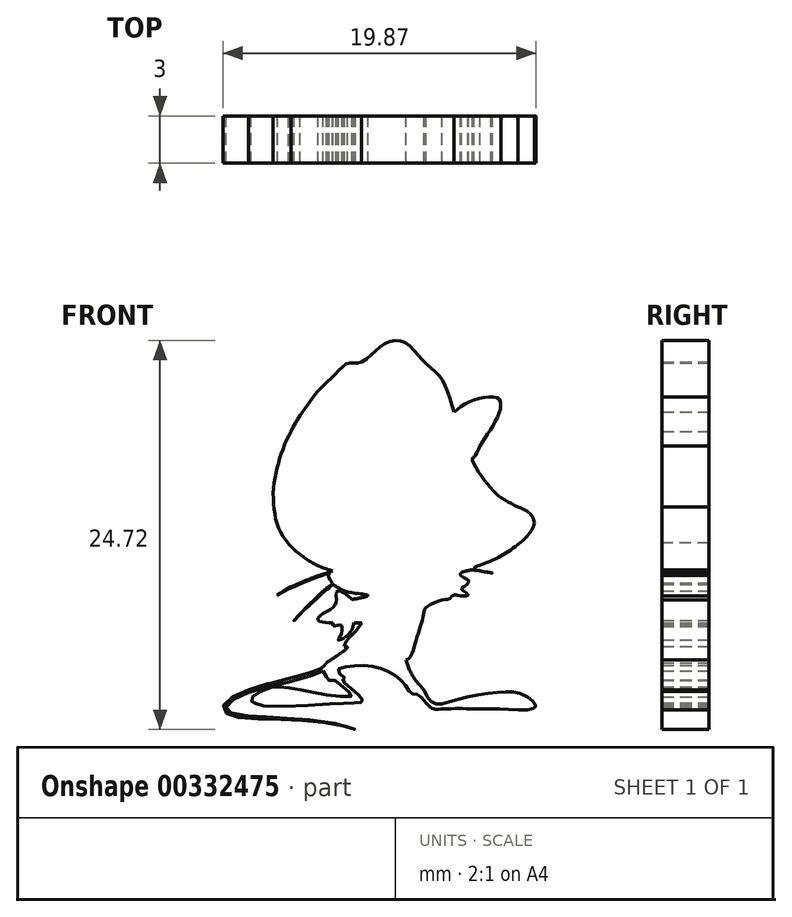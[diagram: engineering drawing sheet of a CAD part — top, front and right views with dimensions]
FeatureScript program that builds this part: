
annotation { "Feature Type Name" : "Feature", "Feature Type Description" : "" }
export const myFeature = defineFeature(function(context is Context, id is Id, definition is map)
    precondition{}
    {
        {
            var Q0;
            Q0=qCreatedBy(makeId("Front.planeOp"),FACE);
            var sketch = newSketch(context, id + "F0", { "sketchPlane" : qUnion([Q0])});
            skLineSegment(sketch, "E0", {"start": v(0, -15.9) * mm, "end": v(0, -15.3) * mm});
            skLineSegment(sketch, "E1", {"start": v(0, -15.3) * mm, "end": v(10.5, -15.15) * mm});
            skLineSegment(sketch, "E2", {"start": v(-10.5, 9.26) * mm, "end": v(-10.5, 18.4) * mm});
            skLineSegment(sketch, "E3", {"start": v(-10.5, 18.4) * mm, "end": v(0, 18.4) * mm});
            skLineSegment(sketch, "E4", {"start": v(0, 18.4) * mm, "end": v(0, 15.3) * mm});
            skLineSegment(sketch, "E5", {"start": v(0, 15.3) * mm, "end": v(10.5, 15.3) * mm});
            skLineSegment(sketch, "E6", {"start": v(10.5, 15.3) * mm, "end": v(10.5, 9.26) * mm});
            skLineSegment(sketch, "E7", {"start": v(-33.45, 0) * mm, "end": v(30.2, 0) * mm});
            skLineSegment(sketch, "E8", {"start": v(0, -15.3) * mm, "end": v(0, -18.4) * mm});
            skLineSegment(sketch, "E9", {"start": v(0, -18.4) * mm, "end": v(-10.5, -18.4) * mm});
            skLineSegment(sketch, "E10", {"start": v(-10.5, -18.4) * mm, "end": v(-10.63, -9.1) * mm});
            skArc(sketch, "E11", {"start": v(-10.5, 9.26) * mm, "mid": v(-14, 0.1) * mm, "end": v(-10.63, -9.1) * mm});
            skLineSegment(sketch, "E12", {"start": v(10.5, -15.15) * mm, "end": v(10.5, -9.26) * mm});
            skArc(sketch, "E13", {"start": v(10.5, -9.26) * mm, "mid": v(14, 0) * mm, "end": v(10.5, 9.26) * mm});
            skFitSpline(sketch, "E14", {"points": [v(-1.65, 11.33) * mm, v(-2.46, 11.25) * mm, v(-3.47, 10.4) * mm, v(-4.37, 9.54) * mm, v(-4.96, 8.75) * mm, v(-5.58, 7.9) * mm, v(-6.13, 6.92) * mm], "startDerivative": vector(-5.08, -3.14) * mm, "endDerivative": vector(-3.13, -6.02) * mm});
            skFitSpline(sketch, "E15", {"points": [v(-6.13, 6.92) * mm, v(-6.64, 5.8) * mm, v(-7, 4.64) * mm, v(-7.25, 3.37) * mm, v(-7.2, 1.97) * mm, v(-6.95, 0.82) * mm, v(-6.34, -0.17) * mm], "startDerivative": vector(-3.31, -6.67) * mm, "endDerivative": vector(4.26, -5.94) * mm});
            skFitSpline(sketch, "E16", {"points": [v(-6.34, -0.17) * mm, v(-5.92, -0.6) * mm, v(-5.29, -1.1) * mm, v(-4.8, -1.42) * mm, v(-4.23, -1.7) * mm, v(-3.51, -1.95) * mm], "startDerivative": vector(2.01, -2.25) * mm, "endDerivative": vector(3.45, -1.18) * mm});
            skFitSpline(sketch, "E17", {"points": [v(-3.51, -1.95) * mm, v(-3.84, -2.08) * mm, v(-4.22, -2.2) * mm, v(-4.99, -2.47) * mm, v(-5.55, -2.7) * mm], "startDerivative": vector(-1.6, -0.67) * mm, "endDerivative": vector(-1.95, -0.8) * mm});
            skFitSpline(sketch, "E18", {"points": [v(-5.55, -2.7) * mm, v(-5.93, -2.87) * mm, v(-6.38, -3.09) * mm, v(-7, -3.49) * mm, v(-6.36, -3.13) * mm, v(-5.5, -2.76) * mm, v(-4.67, -2.4) * mm, v(-3.72, -2.11) * mm], "startDerivative": vector(-3.6, -1.68) * mm, "endDerivative": vector(5.8, 1.6) * mm});
            skFitSpline(sketch, "E19", {"points": [v(-3.72, -2.11) * mm, v(-3.72, -2.42) * mm, v(-3.51, -2.75) * mm, v(-3.76, -2.96) * mm, v(-4.43, -3.54) * mm, v(-5.02, -4.1) * mm, v(-5.55, -4.67) * mm, v(-5.96, -5.1) * mm, v(-5.35, -4.5) * mm, v(-4.64, -3.82) * mm, v(-3.94, -3.18) * mm, v(-3.46, -2.82) * mm], "startDerivative": vector(-1.16, -4.83) * mm, "endDerivative": vector(5.22, 3.74) * mm});
            skFitSpline(sketch, "E20", {"points": [v(-3.46, -2.82) * mm, v(-2.98, -3.1) * mm, v(-2.37, -3.31) * mm, v(-1.25, -3.5) * mm, v(-2.27, -3.76) * mm], "startDerivative": vector(2.4, -1.48) * mm, "endDerivative": vector(-5.67, -1.03) * mm});
            skFitSpline(sketch, "E21", {"points": [v(-2.27, -3.76) * mm, v(-2.63, -3.46) * mm, v(-3.2, -3.22) * mm, v(-3.27, -3.9) * mm, v(-3.61, -4.37) * mm, v(-4.41, -4.94) * mm, v(-4.3, -5.15) * mm, v(-3.46, -5.23) * mm], "startDerivative": vector(-2.37, 2.13) * mm, "endDerivative": vector(5.8, 0.03) * mm});
            skFitSpline(sketch, "E22", {"points": [v(-3.46, -5.23) * mm, v(-3.41, -5.46) * mm, v(-2.98, -5.4) * mm, v(-2.95, -5.97) * mm, v(-3.12, -6.33) * mm, v(-2.64, -6.12) * mm, v(-2.25, -5.61) * mm, v(-2.12, -5.23) * mm], "startDerivative": vector(-0.2, -3) * mm, "endDerivative": vector(0.77, 2.7) * mm});
            skFitSpline(sketch, "E23", {"points": [v(-2.12, -5.23) * mm, v(-1.63, -5.23) * mm], "startDerivative": vector(0.49, 0) * mm, "endDerivative": vector(0.49, 0) * mm});
            skFitSpline(sketch, "E24", {"points": [v(-1.63, -5.23) * mm, v(-2.05, -5.79) * mm, v(-2.6, -6.39) * mm, v(-2.77, -6.74) * mm], "startDerivative": vector(-1.06, -1.55) * mm, "endDerivative": vector(-0.45, -1.27) * mm});
            skFitSpline(sketch, "E25", {"points": [v(-2.77, -6.74) * mm, v(-2.56, -6.8) * mm, v(-3.15, -7.29) * mm, v(-3.87, -7.78) * mm], "startDerivative": vector(1.5, -0.04) * mm, "endDerivative": vector(-1.59, -1.07) * mm});
            skPoint(sketch, "E26.2.internal.snap0", {"position": v(-5.25, -18.4) * mm});
            skFitSpline(sketch, "E26", {"points": [v(-3.87, -7.78) * mm, v(-4.13, -8.05) * mm, v(-5.25, -8.5) * mm, v(-7.3, -9.04) * mm, v(-8.84, -9.49) * mm], "startDerivative": vector(-1.47, -2) * mm, "endDerivative": vector(-5.13, -1.57) * mm});
            skFitSpline(sketch, "E27", {"points": [v(-8.84, -9.49) * mm, v(-9.98, -10.03) * mm, v(-10.4, -10.47) * mm, v(-10.41, -10.81) * mm, v(-10.02, -11.08) * mm, v(-9.2, -11.27) * mm, v(-7.12, -11.36) * mm, v(-5.19, -11.46) * mm, v(-3.1, -11.73) * mm, v(-2.02, -12.02) * mm, v(-3.37, -11.63) * mm, v(-5.92, -11.35) * mm, v(-7.88, -11.21) * mm, v(-9.3, -11.12) * mm, v(-10.16, -10.85) * mm, v(-10.27, -10.7) * mm, v(-10.11, -10.4) * mm, v(-9.65, -10.03) * mm, v(-8.28, -9.49) * mm, v(-6.42, -9.04) * mm, v(-4.43, -8.47) * mm, v(-4.1, -8.3) * mm, v(-4.13, -8.05) * mm], "startDerivative": vector(-25.61, -10.39) * mm, "endDerivative": vector(-3.5, 12.28) * mm});
            skFitSpline(sketch, "E28", {"points": [v(-4.1, -8.3) * mm, v(-3.87, -8.72) * mm, v(-3.76, -8.9) * mm, v(-3.4, -8.88) * mm, v(-2.94, -9.26) * mm, v(-2.27, -9.87) * mm, v(-3.33, -9.88) * mm, v(-5.25, -9.56) * mm, v(-6.66, -9.32) * mm, v(-7.48, -9.38) * mm, v(-8.55, -9.92) * mm, v(-8.66, -10.21) * mm, v(-8.45, -10.29) * mm, v(-8.32, -10.44) * mm, v(-3.98, -10.42) * mm, v(-2.12, -10.32) * mm], "startDerivative": vector(5.59, -9.18) * mm, "endDerivative": vector(14.33, 0.58) * mm});
            skFitSpline(sketch, "E29", {"points": [v(-2.12, -10.32) * mm, v(-1.6, -10.23) * mm, v(-2.12, -9.58) * mm, v(-2.86, -8.86) * mm, v(-2.72, -8.8) * mm, v(-3.16, -8.3) * mm, v(-2.45, -8.01) * mm, v(-0.9, -8.03) * mm, v(0.34, -8.5) * mm, v(1.1, -9.19) * mm, v(1.52, -9.74) * mm, v(1.9, -9.8) * mm, v(2.45, -10.32) * mm], "startDerivative": vector(10.35, 0) * mm, "endDerivative": vector(6.6, -8.47) * mm});
            skFitSpline(sketch, "E30", {"points": [v(2.45, -10.32) * mm, v(2.83, -10.68) * mm, v(3.67, -10.7) * mm, v(5.45, -10.7) * mm, v(6.57, -10.7) * mm], "startDerivative": vector(1.85, -2.43) * mm, "endDerivative": vector(3.92, 0.02) * mm});
            skFitSpline(sketch, "E31", {"points": [v(2.3, -9.51) * mm, v(1.6, -8.65) * mm, v(1.16, -7.6) * mm], "startDerivative": vector(-1.53, 1.65) * mm, "endDerivative": vector(-0.77, 2.16) * mm});
            skFitSpline(sketch, "E32", {"points": [v(1.16, -7.6) * mm, v(0.28, -7.8) * mm, v(-0.55, -7.75) * mm, v(-1.63, -7.25) * mm, v(-2.56, -6.8) * mm], "startDerivative": vector(-3.7, -0.97) * mm, "endDerivative": vector(-3.5, 1.71) * mm});
            skFitSpline(sketch, "E33", {"points": [v(1.16, -7.6) * mm, v(1.4, -7.49) * mm, v(1.82, -6.34) * mm, v(2.16, -5.23) * mm, v(2.3, -4.6) * mm, v(2.45, -4.27) * mm, v(3.44, -3.78) * mm], "startDerivative": vector(2.47, 0.48) * mm, "endDerivative": vector(6.04, 2.27) * mm});
            skFitSpline(sketch, "E34", {"points": [v(3.44, -3.78) * mm, v(3.95, -3.69) * mm, v(4.17, -3.48) * mm, v(4.35, -3.48) * mm, v(4.65, -3.53) * mm, v(5.12, -3.47) * mm, v(4.7, -3.1) * mm, v(4.93, -2.9) * mm, v(5.14, -2.57) * mm, v(4.64, -2.24) * mm, v(4.6, -1.68) * mm, v(4.88, -1.03) * mm, v(4.8, -0.94) * mm, v(3.8, -1.3) * mm, v(3.55, -1.64) * mm, v(3.32, -1.63) * mm, v(2.98, -1.88) * mm, v(1.87, -2.5) * mm, v(1.74, -2.95) * mm, v(0.77, -3.69) * mm], "startDerivative": vector(10.7, 0.47) * mm, "endDerivative": vector(-15.55, -8.76) * mm});
            skFitSpline(sketch, "E35", {"points": [v(0.77, -3.69) * mm, v(0.38, -3.78) * mm, v(0.14, -3.4) * mm, v(-0.15, -3.47) * mm, v(-1.25, -3.5) * mm], "startDerivative": vector(-2, -1.18) * mm, "endDerivative": vector(-3.5, 0.27) * mm});
            skFitSpline(sketch, "E36", {"points": [v(4.64, -2.24) * mm, v(4.64, -2.1) * mm, v(5.38, -1.88) * mm], "startDerivative": vector(-0.16, 0.5) * mm, "endDerivative": vector(1.43, 0.26) * mm});
            skFitSpline(sketch, "E37", {"points": [v(5.38, -1.88) * mm, v(6.65, -2.08) * mm, v(5.49, -1.88) * mm], "startDerivative": vector(3.72, -0.6) * mm, "endDerivative": vector(-3.56, 0.61) * mm});
            skFitSpline(sketch, "E38", {"points": [v(5.49, -1.88) * mm, v(5.49, -1.77) * mm, v(6.61, -1.28) * mm, v(8.29, -0.25) * mm, v(9.31, 1.04) * mm, v(8.96, 1.77) * mm, v(8.29, 2.12) * mm], "startDerivative": vector(-0.7, 1.82) * mm, "endDerivative": vector(-4.71, 1.87) * mm});
            skFitSpline(sketch, "E39", {"points": [v(8.29, 2.12) * mm, v(7.18, 2.72) * mm, v(6.14, 3.84) * mm, v(5.38, 5.18) * mm, v(5.49, 5.3) * mm, v(5.86, 5.98) * mm], "startDerivative": vector(-5, 2.33) * mm, "endDerivative": vector(2.08, 4.84) * mm});
            skFitSpline(sketch, "E40", {"points": [v(5.86, 5.98) * mm, v(6.56, 7.07) * mm, v(7.12, 8.22) * mm, v(7.1, 8.95) * mm, v(6.56, 9.1) * mm, v(5.17, 8.78) * mm, v(4.22, 8.15) * mm], "startDerivative": vector(3.82, 5.77) * mm, "endDerivative": vector(-4.89, -3.98) * mm});
            skFitSpline(sketch, "E41", {"points": [v(-1.65, 11.33) * mm, v(-0.3, 12.42) * mm, v(1.01, 12.6) * mm, v(2.34, 11.33) * mm, v(3.42, 10.27) * mm, v(4.22, 8.15) * mm], "startDerivative": vector(7.13, 3.71) * mm, "endDerivative": vector(3.12, -9.56) * mm});
            skFitSpline(sketch, "E42", {"points": [v(6.57, -10.7) * mm, v(6.69, -10.7) * mm, v(8.58, -10.77) * mm, v(9.42, -10.54) * mm, v(8.58, -9.79) * mm, v(7.03, -9.66) * mm, v(4.34, -10.13) * mm, v(2.97, -10.38) * mm, v(2.3, -9.51) * mm], "startDerivative": vector(1.92, 0.1) * mm, "endDerivative": vector(-4.76, 9.55) * mm});
            skSolve(sketch);
        }
        {
            var Q0;
            {var subQ7=sQuery(id+"F0.wireOp",EDGE,"E21");Q0=makeQuery(id+"F0.imprint","IMPRINT",FACE,{"disambiguationData":[TD([[makeQuery(id+"F0.imprint","IMPRINT",EDGE,{"derivedFrom":subQ7}),1.0]])]});}
            var Q1;
            {var subQ10=sQuery(id+"F0.wireOp",EDGE,"E16");Q1=makeQuery(id+"F0.imprint","IMPRINT",FACE,{"disambiguationData":[TD([[makeQuery(id+"F0.imprint","IMPRINT",EDGE,{"derivedFrom":subQ10}),1.0]])]});}
            var Q2;
            {var subQ1=sQuery(id+"F0.wireOp",EDGE,"E14");Q2=makeQuery(id+"F0.imprint","IMPRINT",FACE,{"disambiguationData":[TD([[makeQuery(id+"F0.imprint","IMPRINT",EDGE,{"derivedFrom":subQ1}),1.0]])]});}
            extrude(context, id + "F1", {"entities" : qUnion([Q0, Q1, Q2]), "depth" : 3 * mm});
        }
        {
            var Q0;
            {var subQ3=sQuery(id+"F0.wireOp",EDGE,"E28");Q0=makeQuery(id+"F0.imprint","IMPRINT",FACE,{"disambiguationData":[TD([[makeQuery(id+"F0.imprint","IMPRINT",EDGE,{"derivedFrom":subQ3}),1.0]])]});}
            extrude(context, id + "F2", {"entities" : qUnion([Q0]), "operationType" : NewBodyOperationType.ADD, "depth" : 3 * mm});
        }
        {
            var Q0;
            {var subQ0=sQuery(id+"F0.wireOp",EDGE,"E27");var subQ1=sQuery(id+"F0.wireOp",EDGE,"E26");var subQ2=makeQuery(id+"F0.imprint","INTERSECT",VERTEX,{"disambiguationData":[OD(0.0)],"derivedFrom":[subQ1,subQ0]});Q0=makeQuery(id+"F0.imprint","IMPRINT",FACE,{"disambiguationData":[TD([[makeQuery(id+"F0.imprint","IMPRINT",EDGE,{"disambiguationData":[TD([[subQ2,1.0]])],"derivedFrom":subQ1}),1.0]])]});}
            extrude(context, id + "F3", {"entities" : qUnion([Q0]), "operationType" : NewBodyOperationType.ADD, "depth" : 3 * mm});
        }
    });
